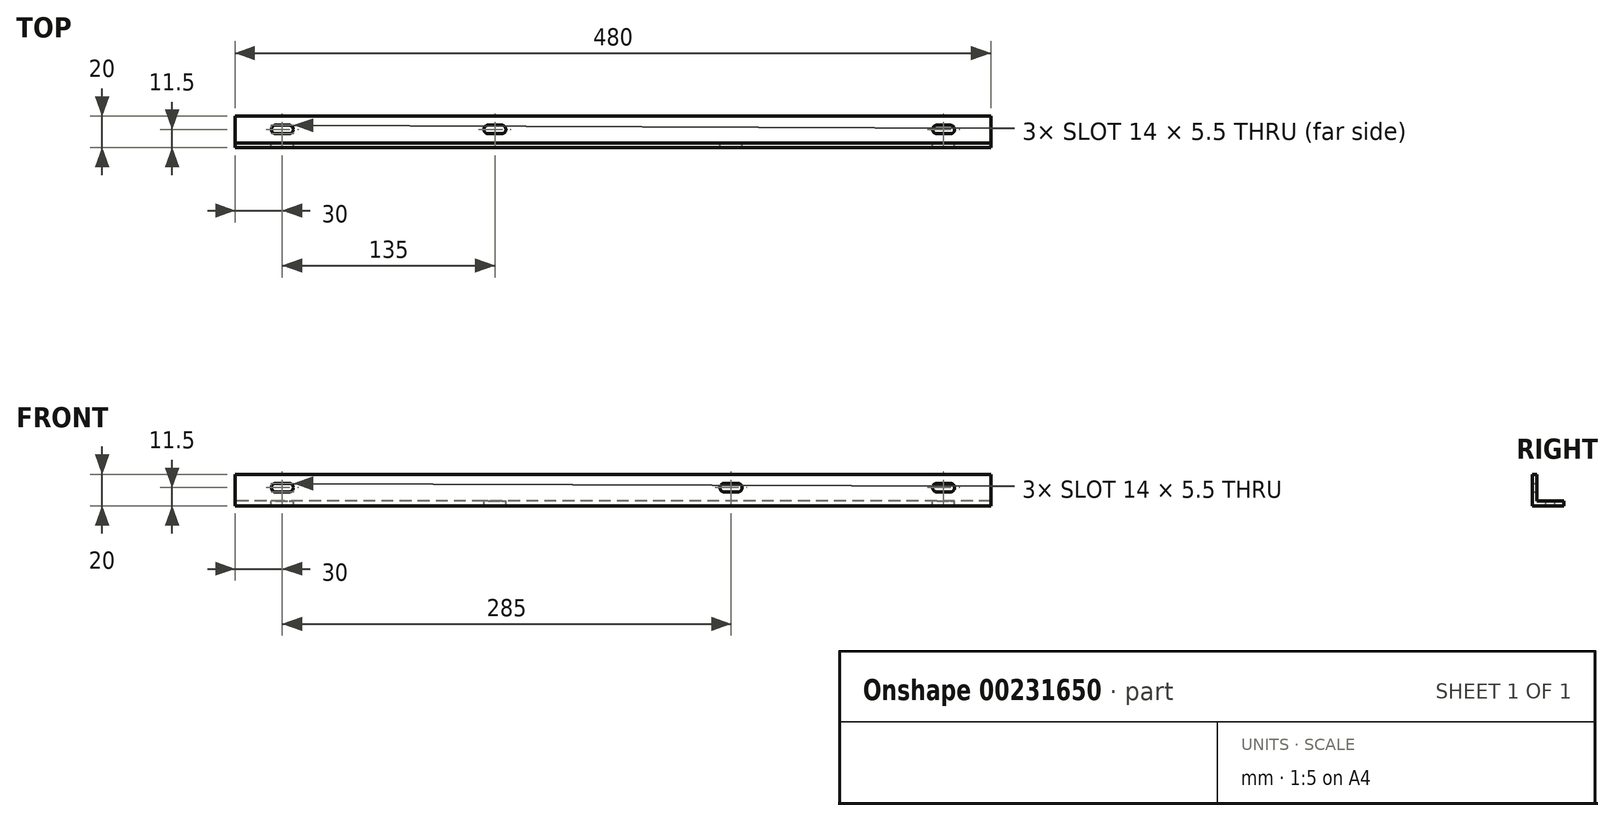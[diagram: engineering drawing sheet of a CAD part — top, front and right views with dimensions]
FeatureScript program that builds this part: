
annotation { "Feature Type Name" : "Feature", "Feature Type Description" : "" }
export const myFeature = defineFeature(function(context is Context, id is Id, definition is map)
    precondition{}
    {
        {
            var Q0;
            Q0=qCreatedBy(makeId("Right.planeOp"),FACE);
            var sketch = newSketch(context, id + "F0", { "sketchPlane" : qUnion([Q0])});
            skLineSegment(sketch, "E0.bottom", {"start": v(0, 0) * mm, "end": v(20, 0) * mm});
            skLineSegment(sketch, "E0.top", {"start": v(3, 3) * mm, "end": v(20, 3) * mm});
            skLineSegment(sketch, "E0.right", {"start": v(20, 0) * mm, "end": v(20, 3) * mm});
            skLineSegment(sketch, "E1.top", {"start": v(0, 20) * mm, "end": v(3, 20) * mm});
            skLineSegment(sketch, "E1.left", {"start": v(0, 0) * mm, "end": v(0, 20) * mm});
            skLineSegment(sketch, "E1.right", {"start": v(3, 3) * mm, "end": v(3, 20) * mm});
            skSolve(sketch);
        }
        {
            var Q0;
            Q0 = qSketchRegion(id + "F0", true);
            extrude(context, id + "F1", {"entities" : qUnion([Q0]), "depth" : 480 * mm});
        }
        {
            var Q0;
            Q0=makeQuery(id+"F1.opExtrude","SWEPT_FACE",FACE,{"disambiguationData":[OSD([sQuery(id+"F0.wireOp",EDGE,"E1.right")])]});
            var sketch = newSketch(context, id + "F2", { "sketchPlane" : qUnion([Q0])});
            skLineSegment(sketch, "E2", {"start": v(-480, 11.5) * mm, "end": v(0, 11.5) * mm, "construction": true});
            skLineSegment(sketch, "E3.bottom", {"start": v(-454.25, 14.25) * mm, "end": v(-445.75, 14.25) * mm});
            skLineSegment(sketch, "E3.top", {"start": v(-454.25, 8.75) * mm, "end": v(-445.75, 8.75) * mm});
            skArc(sketch, "E4", {"start": v(-454.25, 14.25) * mm, "mid": v(-457, 11.5) * mm, "end": v(-454.25, 8.75) * mm});
            skArc(sketch, "E5", {"start": v(-445.75, 8.75) * mm, "mid": v(-443, 11.5) * mm, "end": v(-445.75, 14.25) * mm});
            skLineSegment(sketch, "E6", {"start": v(-450, 14.25) * mm, "end": v(-450, 8.75) * mm, "construction": true});
            skLineSegment(sketch, "E7.bottom", {"start": v(-34.25, 14.25) * mm, "end": v(-25.75, 14.25) * mm});
            skLineSegment(sketch, "E7.top", {"start": v(-34.25, 8.75) * mm, "end": v(-25.75, 8.75) * mm});
            skArc(sketch, "E8", {"start": v(-34.25, 14.25) * mm, "mid": v(-37, 11.5) * mm, "end": v(-34.25, 8.75) * mm});
            skArc(sketch, "E9", {"start": v(-25.75, 8.75) * mm, "mid": v(-23, 11.5) * mm, "end": v(-25.75, 14.25) * mm});
            skLineSegment(sketch, "E10", {"start": v(-30, 14.25) * mm, "end": v(-30, 8.75) * mm, "construction": true});
            skLineSegment(sketch, "E11.bottom", {"start": v(-319.25, 14.25) * mm, "end": v(-310.75, 14.25) * mm});
            skLineSegment(sketch, "E11.top", {"start": v(-319.25, 8.75) * mm, "end": v(-310.75, 8.75) * mm});
            skArc(sketch, "E12", {"start": v(-319.25, 14.25) * mm, "mid": v(-322, 11.5) * mm, "end": v(-319.25, 8.75) * mm});
            skArc(sketch, "E13", {"start": v(-310.75, 8.75) * mm, "mid": v(-308, 11.5) * mm, "end": v(-310.75, 14.25) * mm});
            skLineSegment(sketch, "E14", {"start": v(-315, 14.25) * mm, "end": v(-315, 8.75) * mm, "construction": true});
            skSolve(sketch);
        }
        {
            var Q0;
            Q0 = qSketchRegion(id + "F2", true);
            extrude(context, id + "F3", {"entities" : qUnion([Q0]), "operationType" : NewBodyOperationType.REMOVE, "oppositeDirection" : true, "depth" : 3 * mm});
        }
        {
            var Q0;
            Q0=makeQuery(id+"F1.opExtrude","SWEPT_FACE",FACE,{"disambiguationData":[OSD([sQuery(id+"F0.wireOp",EDGE,"E0.top")])]});
            var sketch = newSketch(context, id + "F4", { "sketchPlane" : qUnion([Q0])});
            skLineSegment(sketch, "E15", {"start": v(0, 11.5) * mm, "end": v(480, 11.5) * mm, "construction": true});
            skLineSegment(sketch, "E16.bottom", {"start": v(445.75, 14.25) * mm, "end": v(454.25, 14.25) * mm});
            skLineSegment(sketch, "E16.top", {"start": v(445.75, 8.75) * mm, "end": v(454.25, 8.75) * mm});
            skArc(sketch, "E17", {"start": v(445.75, 14.25) * mm, "mid": v(443, 11.5) * mm, "end": v(445.75, 8.75) * mm});
            skArc(sketch, "E18", {"start": v(454.25, 8.75) * mm, "mid": v(457, 11.5) * mm, "end": v(454.25, 14.25) * mm});
            skLineSegment(sketch, "E19", {"start": v(450, 14.25) * mm, "end": v(450, 8.75) * mm, "construction": true});
            skLineSegment(sketch, "E20.bottom", {"start": v(160.75, 14.25) * mm, "end": v(169.25, 14.25) * mm});
            skLineSegment(sketch, "E20.top", {"start": v(160.75, 8.75) * mm, "end": v(169.25, 8.75) * mm});
            skArc(sketch, "E21", {"start": v(160.75, 14.25) * mm, "mid": v(158, 11.5) * mm, "end": v(160.75, 8.75) * mm});
            skArc(sketch, "E22", {"start": v(169.25, 8.75) * mm, "mid": v(172, 11.5) * mm, "end": v(169.25, 14.25) * mm});
            skLineSegment(sketch, "E23", {"start": v(165, 14.25) * mm, "end": v(165, 8.75) * mm, "construction": true});
            skLineSegment(sketch, "E24.bottom", {"start": v(25.75, 14.25) * mm, "end": v(34.25, 14.25) * mm});
            skLineSegment(sketch, "E24.top", {"start": v(25.75, 8.75) * mm, "end": v(34.25, 8.75) * mm});
            skArc(sketch, "E25", {"start": v(25.75, 14.25) * mm, "mid": v(23, 11.5) * mm, "end": v(25.75, 8.75) * mm});
            skArc(sketch, "E26", {"start": v(34.25, 8.75) * mm, "mid": v(37, 11.5) * mm, "end": v(34.25, 14.25) * mm});
            skLineSegment(sketch, "E27", {"start": v(30, 14.25) * mm, "end": v(30, 8.75) * mm, "construction": true});
            skSolve(sketch);
        }
        {
            var Q0;
            Q0 = qSketchRegion(id + "F4", true);
            extrude(context, id + "F5", {"entities" : qUnion([Q0]), "operationType" : NewBodyOperationType.REMOVE, "oppositeDirection" : true, "depth" : 3 * mm});
        }
    });
